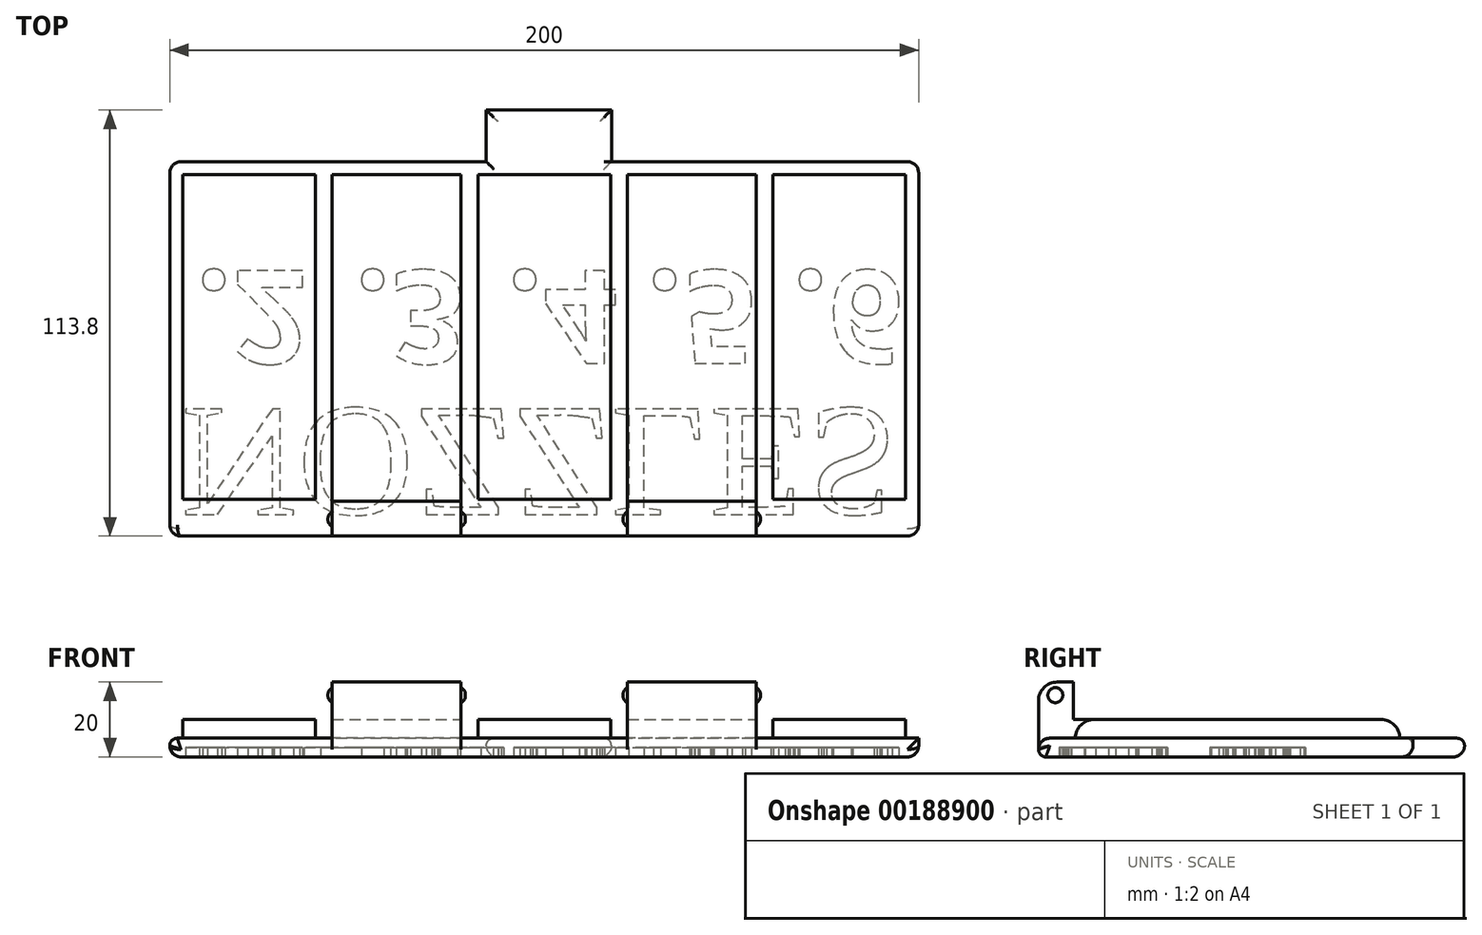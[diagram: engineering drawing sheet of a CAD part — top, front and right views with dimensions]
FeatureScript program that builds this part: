
annotation { "Feature Type Name" : "Feature", "Feature Type Description" : "" }
export const myFeature = defineFeature(function(context is Context, id is Id, definition is map)
    precondition{}
    {
        {
            var Q0;
            Q0=qCreatedBy(makeId("Top.planeOp"),FACE);
            var sketch = newSketch(context, id + "F0", { "sketchPlane" : qUnion([Q0])});
            skLineSegment(sketch, "E0.bottom", {"start": v(-103.4, 30.23) * mm, "end": v(96.6, 30.23) * mm});
            skLineSegment(sketch, "E0.top", {"start": v(-103.4, -69.77) * mm, "end": v(96.6, -69.77) * mm});
            skLineSegment(sketch, "E0.left", {"start": v(-103.4, 30.23) * mm, "end": v(-103.4, -69.77) * mm});
            skLineSegment(sketch, "E0.right", {"start": v(96.6, 30.23) * mm, "end": v(96.6, -69.77) * mm});
            skLineSegment(sketch, "E1.bottom", {"start": v(-18.87, 30.23) * mm, "end": v(14.56, 30.23) * mm});
            skLineSegment(sketch, "E1.top", {"start": v(-18.87, 44.03) * mm, "end": v(14.56, 44.03) * mm});
            skLineSegment(sketch, "E1.left", {"start": v(-18.87, 30.23) * mm, "end": v(-18.87, 44.03) * mm});
            skLineSegment(sketch, "E1.right", {"start": v(14.56, 30.23) * mm, "end": v(14.56, 44.03) * mm});
            skSolve(sketch);
        }
        {
            var Q0;
            Q0=makeQuery(id+"F0.imprint","IMPRINT",FACE,{"disambiguationData":[TD([[makeQuery(id+"F0.imprint","IMPRINT",EDGE,{"derivedFrom":sQuery(id+"F0.wireOp",EDGE,"E0.bottom")}),-1.0]])]});
            var sketch = newSketch(context, id + "F1", { "sketchPlane" : qUnion([Q0])});
            skLineSegment(sketch, "E2.bottom", {"start": v(-99.9, 26.73) * mm, "end": v(-64.5, 26.73) * mm});
            skLineSegment(sketch, "E2.top", {"start": v(-99.9, -59.9) * mm, "end": v(-64.5, -59.9) * mm});
            skLineSegment(sketch, "E2.left", {"start": v(-99.9, 26.73) * mm, "end": v(-99.9, -59.9) * mm});
            skLineSegment(sketch, "E2.right", {"start": v(-64.5, 26.73) * mm, "end": v(-64.5, -59.9) * mm});
            skLineSegment(sketch, "E3.bottom", {"start": v(-60, 26.73) * mm, "end": v(-25.6, 26.73) * mm});
            skLineSegment(sketch, "E3.top", {"start": v(-60, -69.77) * mm, "end": v(-25.6, -69.77) * mm});
            skLineSegment(sketch, "E3.left", {"start": v(-60, 26.73) * mm, "end": v(-60, -69.77) * mm});
            skLineSegment(sketch, "E3.right", {"start": v(-25.6, 26.73) * mm, "end": v(-25.6, -69.77) * mm});
            skLineSegment(sketch, "E4.bottom", {"start": v(-21.1, 26.73) * mm, "end": v(14.3, 26.73) * mm});
            skLineSegment(sketch, "E4.top", {"start": v(-21.1, -59.9) * mm, "end": v(14.3, -59.9) * mm});
            skLineSegment(sketch, "E4.left", {"start": v(-21.1, 26.73) * mm, "end": v(-21.1, -59.9) * mm});
            skLineSegment(sketch, "E4.right", {"start": v(14.3, 26.73) * mm, "end": v(14.3, -59.9) * mm});
            skLineSegment(sketch, "E5.bottom", {"start": v(18.8, 26.73) * mm, "end": v(53.2, 26.73) * mm});
            skLineSegment(sketch, "E5.top", {"start": v(18.8, -69.77) * mm, "end": v(53.2, -69.77) * mm});
            skLineSegment(sketch, "E5.left", {"start": v(18.8, 26.73) * mm, "end": v(18.8, -69.77) * mm});
            skLineSegment(sketch, "E5.right", {"start": v(53.2, 26.73) * mm, "end": v(53.2, -69.77) * mm});
            skLineSegment(sketch, "E6.bottom", {"start": v(57.7, 26.73) * mm, "end": v(93.1, 26.73) * mm});
            skLineSegment(sketch, "E6.top", {"start": v(57.7, -59.9) * mm, "end": v(93.1, -59.9) * mm});
            skLineSegment(sketch, "E6.left", {"start": v(57.7, 26.73) * mm, "end": v(57.7, -59.9) * mm});
            skLineSegment(sketch, "E6.right", {"start": v(93.1, 26.73) * mm, "end": v(93.1, -59.9) * mm});
            skSolve(sketch);
        }
        {
            var Q0;
            Q0 = qSketchRegion(id + "F0", true);
            extrude(context, id + "F2", {"entities" : qUnion([Q0]), "depth" : 5 * mm});
        }
        {
            var Q0;
            Q0 = qSketchRegion(id + "F1", true);
            extrude(context, id + "F3", {"entities" : qUnion([Q0]), "operationType" : NewBodyOperationType.ADD, "depth" : 10 * mm});
        }
        {
            var Q0;
            Q0=makeQuery(id+"F3.opExtrude","CAP_EDGE",EDGE,{"disambiguationData":[OSD([sQuery(id+"F1.wireOp",EDGE,"E2.top")])],"isStart":false});
            var Q1;
            Q1=makeQuery(id+"F3.opExtrude","CAP_EDGE",EDGE,{"disambiguationData":[OSD([sQuery(id+"F1.wireOp",EDGE,"E4.top")])],"isStart":false});
            var Q2;
            Q2=makeQuery(id+"F3.opExtrude","CAP_EDGE",EDGE,{"disambiguationData":[OSD([sQuery(id+"F1.wireOp",EDGE,"E6.top")])],"isStart":false});
            var Q3;
            Q3=makeQuery(id+"F3.opExtrude","CAP_EDGE",EDGE,{"disambiguationData":[OSD([sQuery(id+"F1.wireOp",EDGE,"E2.bottom")])],"isStart":false});
            var Q4;
            Q4=makeQuery(id+"F3.opExtrude","CAP_EDGE",EDGE,{"disambiguationData":[OSD([sQuery(id+"F1.wireOp",EDGE,"E3.bottom")])],"isStart":false});
            var Q5;
            Q5=makeQuery(id+"F3.opExtrude","CAP_EDGE",EDGE,{"disambiguationData":[OSD([sQuery(id+"F1.wireOp",EDGE,"E4.bottom")])],"isStart":false});
            var Q6;
            Q6=makeQuery(id+"F3.opExtrude","CAP_EDGE",EDGE,{"disambiguationData":[OSD([sQuery(id+"F1.wireOp",EDGE,"E5.bottom")])],"isStart":false});
            var Q7;
            Q7=makeQuery(id+"F3.opExtrude","CAP_EDGE",EDGE,{"disambiguationData":[OSD([sQuery(id+"F1.wireOp",EDGE,"E6.bottom")])],"isStart":false});
            fillet(context, id + "F4", {"entities" : qUnion([Q0, Q1, Q2, Q3, Q4, Q5, Q6, Q7]), "radius" : 5 * mm, "tangentPropagation" : true, "allowEdgeOverflow" : false});
        }
        {
            var Q0;
            Q0=makeQuery(id+"F2.opExtrude","CAP_EDGE",EDGE,{"disambiguationData":[OSD([sQuery(id+"F0.wireOp",EDGE,"E0.left")])],"isStart":true});
            var Q1;
            Q1=makeQuery(id+"F2.opExtrude","SWEPT_EDGE",EDGE,{"disambiguationData":[OSD([sQuery(id+"F0.wireOp",EDGE,"E0.top"),sQuery(id+"F0.wireOp",EDGE,"E0.left")])]});
            var Q2;
            Q2=makeQuery(id+"F2.opExtrude","SWEPT_EDGE",EDGE,{"disambiguationData":[OSD([sQuery(id+"F0.wireOp",EDGE,"E0.top"),sQuery(id+"F0.wireOp",EDGE,"E0.right")])]});
            var Q3;
            Q3=makeQuery(id+"F2.opExtrude","CAP_EDGE",EDGE,{"disambiguationData":[OSD([sQuery(id+"F0.wireOp",EDGE,"E0.right")])],"isStart":true});
            var Q4;
            Q4=makeQuery(id+"F2.opExtrude","SWEPT_EDGE",EDGE,{"disambiguationData":[OSD([sQuery(id+"F0.wireOp",EDGE,"E0.bottom"),sQuery(id+"F0.wireOp",EDGE,"E0.right")])]});
            var Q5;
            Q5=makeQuery(id+"F2.opExtrude","CAP_EDGE",EDGE,{"disambiguationData":[OSD([sQuery(id+"F0.wireOp",EDGE,"E0.bottom")])],"isStart":true});
            var Q6;
            Q6=makeQuery(id+"F2.opExtrude","SWEPT_EDGE",EDGE,{"disambiguationData":[OSD([sQuery(id+"F0.wireOp",EDGE,"E0.bottom"),sQuery(id+"F0.wireOp",EDGE,"E0.left")])]});
            var Q7;
            Q7=makeQuery(id+"F2.opExtrude","CAP_EDGE",EDGE,{"disambiguationData":[OSD([sQuery(id+"F0.wireOp",EDGE,"E1.right")])],"isStart":true});
            var Q8;
            Q8=makeQuery(id+"F2.opExtrude","CAP_EDGE",EDGE,{"disambiguationData":[OSD([sQuery(id+"F0.wireOp",EDGE,"E1.top")])],"isStart":true});
            var Q9;
            Q9=makeQuery(id+"F2.opExtrude","CAP_EDGE",EDGE,{"disambiguationData":[OSD([sQuery(id+"F0.wireOp",EDGE,"E1.left")])],"isStart":true});
            var Q10;
            {var subQ0=sQuery(id+"F0.wireOp",EDGE,"E0.right");var subQ1=sQuery(id+"F0.wireOp",EDGE,"E0.top");Q10=makeQuery(id+"F3.boolean.opBoolean","SPLIT",EDGE,{"disambiguationData":[TD([makeQuery(id+"F2.opExtrude","SWEPT_FACE",FACE,{"disambiguationData":[OSD([subQ0])]})])],"derivedFrom":makeQuery(id+"F2.opExtrude","CAP_EDGE",EDGE,{"disambiguationData":[OSD([subQ1])],"isStart":false})});}
            var Q11;
            {var subQ0=sQuery(id+"F0.wireOp",EDGE,"E0.top");Q11=makeQuery(id+"F3.boolean.opBoolean","SPLIT",EDGE,{"disambiguationData":[TD([makeQuery(id+"F3.opExtrude","SWEPT_FACE",FACE,{"disambiguationData":[OSD([sQuery(id+"F1.wireOp",EDGE,"E3.right")])]})])],"derivedFrom":makeQuery(id+"F2.opExtrude","CAP_EDGE",EDGE,{"disambiguationData":[OSD([subQ0])],"isStart":false})});}
            var Q12;
            {var subQ0=sQuery(id+"F0.wireOp",EDGE,"E0.left");var subQ1=sQuery(id+"F0.wireOp",EDGE,"E0.top");Q12=makeQuery(id+"F3.boolean.opBoolean","SPLIT",EDGE,{"disambiguationData":[TD([makeQuery(id+"F2.opExtrude","SWEPT_FACE",FACE,{"disambiguationData":[OSD([subQ0])]})])],"derivedFrom":makeQuery(id+"F2.opExtrude","CAP_EDGE",EDGE,{"disambiguationData":[OSD([subQ1])],"isStart":false})});}
            fillet(context, id + "F5", {"entities" : qUnion([Q0, Q1, Q2, Q3, Q4, Q5, Q6, Q7, Q8, Q9, Q10, Q11, Q12]), "radius" : 3 * mm, "tangentPropagation" : true, "allowEdgeOverflow" : false});
        }
        {
            var Q0;
            Q0=makeQuery(id+"F2.opExtrude","CAP_FACE",FACE,{"disambiguationData":[OSD([sQuery(id+"F0.wireOp",EDGE,"E0.bottom"),sQuery(id+"F0.wireOp",EDGE,"E0.top"),sQuery(id+"F0.wireOp",EDGE,"E0.left"),sQuery(id+"F0.wireOp",EDGE,"E0.right")])],"isStart":true});
            var sketch = newSketch(context, id + "F6", { "sketchPlane" : qUnion([Q0])});
            skLineSegment(sketch, "E7.left", {"start": v(-96.6, 23.86) * mm, "end": v(-96.6, -1.14) * mm});
            skLineSegment(sketch, "E7.right", {"start": v(-60.2, 23.86) * mm, "end": v(-60.2, -1.14) * mm});
            skLineSegment(sketch, "E8.left", {"start": v(-57.2, 23.86) * mm, "end": v(-57.2, -1.14) * mm});
            skLineSegment(sketch, "E8.right", {"start": v(-20.8, 23.86) * mm, "end": v(-20.8, -1.14) * mm});
            skLineSegment(sketch, "E9.left", {"start": v(-17.8, 23.86) * mm, "end": v(-17.8, -1.14) * mm});
            skLineSegment(sketch, "E9.right", {"start": v(18.6, 23.86) * mm, "end": v(18.6, -1.14) * mm});
            skLineSegment(sketch, "E10.right", {"start": v(58, 23.86) * mm, "end": v(58, -1.14) * mm});
            skLineSegment(sketch, "E11.left", {"start": v(61, 23.86) * mm, "end": v(61, -1.14) * mm});
            skLineSegment(sketch, "E12", {"start": v(-96.6, 23.86) * mm, "end": v(58, 23.86) * mm, "construction": true});
            skLineSegment(sketch, "E13", {"start": v(-96.6, -1.14) * mm, "end": v(61, -1.14) * mm, "construction": true});
            skText(sketch, "E14", { "text": ".2", "fontName": "OpenSans-Bold.ttf"});
            skText(sketch, "E15", { "text": ".3", "fontName": "OpenSans-Bold.ttf"});
            skText(sketch, "E16", { "text": ".4", "fontName": "OpenSans-Bold.ttf"});
            skText(sketch, "E17", { "text": ".5", "fontName": "OpenSans-Bold.ttf"});
            skText(sketch, "E18", { "text": ".6", "fontName": "OpenSans-Bold.ttf"});
            skPoint(sketch, "E19.orphan", {"position": v(-60.2, -46.1) * mm});
            skPoint(sketch, "E9.top.end.orphan", {"position": v(18.6, -46.1) * mm});
            skPoint(sketch, "E8.top.end.orphan", {"position": v(-20.8, -46.1) * mm});
            skPoint(sketch, "E20.orphan", {"position": v(58, -46.1) * mm});
            skPoint(sketch, "E21.orphan", {"position": v(58, 46.05) * mm});
            skPoint(sketch, "E11.bottom.start.orphan", {"position": v(61, 46.05) * mm});
            skPoint(sketch, "E22.orphan", {"position": v(97.4, -46.1) * mm});
            skText(sketch, "E23", { "text": "NOZZLES", "fontName": "Tinos-Regular.ttf"});
            const initialGuessF6  = {"E14": [-0.0966, -0.00114, 1, 0, 0.025], "E15": [-0.05416, -0.00114, 1, 0, 0.025], "E16": [-0.01353, -0.00114, 1, 0, 0.025], "E17": [0.02382, -0.00114, 1, 0, 0.025], "E18": [0.06272, -0.00114, 1, 0, 0.025], "E23": [-0.1004, 0.03577, 1, 0, 0.031]};
            skSetInitialGuess(sketch, initialGuessF6);
            skSolve(sketch);
        }
        {
            var Q0;
            Q0 = qSketchRegion(id + "F6", true);
            extrude(context, id + "F7", {"entities" : qUnion([Q0]), "operationType" : NewBodyOperationType.REMOVE, "oppositeDirection" : true, "depth" : 2.5 * mm});
        }
        {
            var Q0;
            Q0=makeQuery(id+"F3.opExtrude","CAP_FACE",FACE,{"disambiguationData":[OSD([sQuery(id+"F1.wireOp",EDGE,"E5.bottom"),sQuery(id+"F1.wireOp",EDGE,"E5.top"),sQuery(id+"F1.wireOp",EDGE,"E5.left"),sQuery(id+"F1.wireOp",EDGE,"E5.right")])],"isStart":false});
            var sketch = newSketch(context, id + "F8", { "sketchPlane" : qUnion([Q0])});
            skLineSegment(sketch, "E24.bottom", {"start": v(-25.6, -69.77) * mm, "end": v(-29.6, -69.77) * mm});
            skLineSegment(sketch, "E24.top", {"start": v(-25.6, -60.4) * mm, "end": v(-29.6, -60.4) * mm});
            skLineSegment(sketch, "E24.left", {"start": v(-25.6, -69.77) * mm, "end": v(-25.6, -60.4) * mm});
            skLineSegment(sketch, "E24.right", {"start": v(-60, -69.77) * mm, "end": v(-60, -60.4) * mm});
            skLineSegment(sketch, "E25.trimOffspring", {"start": v(-32.6, -69.77) * mm, "end": v(-53, -69.77) * mm});
            skLineSegment(sketch, "E26.trimOffspring", {"start": v(-32.6, -60.4) * mm, "end": v(-53, -60.4) * mm});
            skLineSegment(sketch, "E27.trimOffspring", {"start": v(-56, -60.4) * mm, "end": v(-60, -60.4) * mm});
            skLineSegment(sketch, "E28.trimOffspring", {"start": v(-56, -69.77) * mm, "end": v(-60, -69.77) * mm});
            skLineSegment(sketch, "E29", {"start": v(-56, -60.4) * mm, "end": v(-53, -60.4) * mm});
            skLineSegment(sketch, "E30", {"start": v(-53, -69.77) * mm, "end": v(-56, -69.77) * mm});
            skLineSegment(sketch, "E31", {"start": v(-32.6, -60.4) * mm, "end": v(-29.6, -60.4) * mm});
            skLineSegment(sketch, "E32", {"start": v(-29.6, -69.77) * mm, "end": v(-32.6, -69.77) * mm});
            skLineSegment(sketch, "E33.bottom", {"start": v(18.8, -60.4) * mm, "end": v(53.2, -60.4) * mm});
            skLineSegment(sketch, "E33.top", {"start": v(18.8, -69.77) * mm, "end": v(53.2, -69.77) * mm});
            skLineSegment(sketch, "E33.left", {"start": v(18.8, -60.4) * mm, "end": v(18.8, -69.77) * mm});
            skLineSegment(sketch, "E33.right", {"start": v(53.2, -60.4) * mm, "end": v(53.2, -69.77) * mm});
            skSolve(sketch);
        }
        {
            var Q0;
            Q0 = qSketchRegion(id + "F8", true);
            extrude(context, id + "F9", {"entities" : qUnion([Q0]), "operationType" : NewBodyOperationType.ADD, "depth" : 10 * mm});
        }
        {
            var Q0;
            Q0=makeQuery(id+"F9.opExtrude","CAP_EDGE",EDGE,{"disambiguationData":[OSD([sQuery(id+"F8.wireOp",EDGE,"E24.bottom")])],"isStart":false});
            var Q1;
            Q1=makeQuery(id+"F9.opExtrude","CAP_EDGE",EDGE,{"disambiguationData":[OSD([sQuery(id+"F8.wireOp",EDGE,"fa0df908-ae73-434e-80fb-e9a63f663edb.bottom")])],"isStart":false});
            var Q2;
            Q2=makeQuery(id+"F9.opExtrude","CAP_EDGE",EDGE,{"disambiguationData":[OSD([sQuery(id+"F8.wireOp",EDGE,"E25.trimOffspring")])],"isStart":false});
            var Q3;
            Q3=makeQuery(id+"F9.opExtrude","CAP_EDGE",EDGE,{"disambiguationData":[OSD([sQuery(id+"F8.wireOp",EDGE,"E28.trimOffspring")])],"isStart":false});
            var Q4;
            Q4=makeQuery(id+"F9.opExtrude","CAP_EDGE",EDGE,{"disambiguationData":[OSD([sQuery(id+"F8.wireOp",EDGE,"31049aec-f189-481b-be80-5d468b2427ca.trimOffspring")])],"isStart":false});
            var Q5;
            Q5=makeQuery(id+"F9.opExtrude","CAP_EDGE",EDGE,{"disambiguationData":[OSD([sQuery(id+"F8.wireOp",EDGE,"0924c1d6-45e6-4c9e-b806-b59c634f07b1.trimOffspring")])],"isStart":false});
            var Q6;
            Q6=makeQuery(id+"F9.opExtrude","CAP_EDGE",EDGE,{"disambiguationData":[OSD([sQuery(id+"F8.wireOp",EDGE,"E33.top")])],"isStart":false});
            fillet(context, id + "F10", {"entities" : qUnion([Q0, Q1, Q2, Q3, Q4, Q5, Q6]), "radius" : 5 * mm, "tangentPropagation" : true, "allowEdgeOverflow" : false});
        }
        {
            var Q0;
            Q0=makeQuery(id+"F9.boolean.opBoolean","MERGE",FACE,{"derivedFrom":[makeQuery(id+"F3.opExtrude","SWEPT_FACE",FACE,{"disambiguationData":[OSD([sQuery(id+"F1.wireOp",EDGE,"E3.left")])]}),makeQuery(id+"F9.opExtrude","SWEPT_FACE",FACE,{"disambiguationData":[OSD([sQuery(id+"F8.wireOp",EDGE,"E24.right")])]})]});
            var sketch = newSketch(context, id + "F11", { "sketchPlane" : qUnion([Q0])});
            skCircle(sketch, "E34", {"center": v(65.27, 16.5) * mm, "radius": 2 * mm});
            skSolve(sketch);
        }
        {
            var Q0;
            Q0=makeQuery(id+"F9.boolean.opBoolean","MERGE",FACE,{"derivedFrom":[makeQuery(id+"F3.opExtrude","SWEPT_FACE",FACE,{"disambiguationData":[OSD([sQuery(id+"F1.wireOp",EDGE,"E3.right")])]}),makeQuery(id+"F9.opExtrude","SWEPT_FACE",FACE,{"disambiguationData":[OSD([sQuery(id+"F8.wireOp",EDGE,"E24.left")])]})]});
            var sketch = newSketch(context, id + "F12", { "sketchPlane" : qUnion([Q0])});
            skCircle(sketch, "E35", {"center": v(-65.27, 16.5) * mm, "radius": 2 * mm});
            skSolve(sketch);
        }
        {
            var Q0;
            Q0=makeQuery(id+"F9.boolean.opBoolean","MERGE",FACE,{"derivedFrom":[makeQuery(id+"F3.opExtrude","SWEPT_FACE",FACE,{"disambiguationData":[OSD([sQuery(id+"F1.wireOp",EDGE,"E5.right")])]}),makeQuery(id+"F9.opExtrude","SWEPT_FACE",FACE,{"disambiguationData":[OSD([sQuery(id+"F8.wireOp",EDGE,"fa0df908-ae73-434e-80fb-e9a63f663edb.left")])]})]});
            var sketch = newSketch(context, id + "F13", { "sketchPlane" : qUnion([Q0])});
            skCircle(sketch, "E36", {"center": v(-65.27, 16.5) * mm, "radius": 2 * mm});
            skSolve(sketch);
        }
        {
            var Q0;
            Q0=makeQuery(id+"F9.boolean.opBoolean","MERGE",FACE,{"derivedFrom":[makeQuery(id+"F3.opExtrude","SWEPT_FACE",FACE,{"disambiguationData":[OSD([sQuery(id+"F1.wireOp",EDGE,"E5.left")])]}),makeQuery(id+"F9.opExtrude","SWEPT_FACE",FACE,{"disambiguationData":[OSD([sQuery(id+"F8.wireOp",EDGE,"fa0df908-ae73-434e-80fb-e9a63f663edb.right")])]})]});
            var sketch = newSketch(context, id + "F14", { "sketchPlane" : qUnion([Q0])});
            skCircle(sketch, "E37", {"center": v(65.27, 16.5) * mm, "radius": 2 * mm});
            skSolve(sketch);
        }
        {
            var Q0;
            Q0=makeQuery(id+"F11.imprint","IMPRINT",FACE,{"disambiguationData":[TD([[makeQuery(id+"F11.imprint","IMPRINT",EDGE,{"derivedFrom":sQuery(id+"F11.wireOp",EDGE,"E34")}),1.0]])]});
            var Q1;
            Q1=makeQuery(id+"F14.imprint","IMPRINT",FACE,{"disambiguationData":[TD([[makeQuery(id+"F14.imprint","IMPRINT",EDGE,{"derivedFrom":sQuery(id+"F14.wireOp",EDGE,"E37")}),1.0]])]});
            var Q2;
            Q2=makeQuery(id+"F13.imprint","IMPRINT",FACE,{"disambiguationData":[TD([[makeQuery(id+"F13.imprint","IMPRINT",EDGE,{"derivedFrom":sQuery(id+"F13.wireOp",EDGE,"E36")}),1.0]])]});
            var Q3;
            Q3=makeQuery(id+"F12.imprint","IMPRINT",FACE,{"disambiguationData":[TD([[makeQuery(id+"F12.imprint","IMPRINT",EDGE,{"derivedFrom":sQuery(id+"F12.wireOp",EDGE,"E35")}),1.0]])]});
            extrude(context, id + "F15", {"entities" : qUnion([Q0, Q1, Q2, Q3]), "operationType" : NewBodyOperationType.ADD, "endBound" : BoundingType.SYMMETRIC, "depth" : 2.3 * mm});
        }
        {
            var Q0;
            Q0=makeQuery(id+"F15.opExtrude","CAP_EDGE",EDGE,{"disambiguationData":[OSD([sQuery(id+"F11.wireOp",EDGE,"E34")])],"isStart":false});
            var Q1;
            Q1=makeQuery(id+"F15.opExtrude","CAP_EDGE",EDGE,{"disambiguationData":[OSD([sQuery(id+"F14.wireOp",EDGE,"E37")])],"isStart":false});
            var Q2;
            Q2=makeQuery(id+"F15.opExtrude","CAP_EDGE",EDGE,{"disambiguationData":[OSD([sQuery(id+"F12.wireOp",EDGE,"E35")])],"isStart":true});
            var Q3;
            Q3=makeQuery(id+"F15.opExtrude","CAP_EDGE",EDGE,{"disambiguationData":[OSD([sQuery(id+"F13.wireOp",EDGE,"E36")])],"isStart":true});
            fillet(context, id + "F16", {"entities" : qUnion([Q0, Q1, Q2, Q3]), "radius" : 2 * mm, "tangentPropagation" : true, "allowEdgeOverflow" : false});
        }
        {
            var Q0;
            Q0=makeQuery(id+"F2.opExtrude","CAP_EDGE",EDGE,{"disambiguationData":[OSD([sQuery(id+"F0.wireOp",EDGE,"E0.left")])],"isStart":false});
            var Q1;
            {var subQ0=sQuery(id+"F0.wireOp",EDGE,"E0.left");var subQ1=sQuery(id+"F0.wireOp",EDGE,"E0.top");Q1=makeQuery(id+"F3.boolean.opBoolean","SPLIT",EDGE,{"disambiguationData":[TD([makeQuery(id+"F2.opExtrude","SWEPT_FACE",FACE,{"disambiguationData":[OSD([subQ0])]})])],"derivedFrom":makeQuery(id+"F2.opExtrude","CAP_EDGE",EDGE,{"disambiguationData":[OSD([subQ1])],"isStart":false})});}
            var Q2;
            {var subQ0=sQuery(id+"F0.wireOp",EDGE,"E0.left");var subQ1=sQuery(id+"F0.wireOp",EDGE,"E0.top");Q2=makeQuery(id+"F5.opFillet","BLEND_EDGE",EDGE,{"blendedFrom":[makeQuery(id+"F2.opExtrude","SWEPT_EDGE",EDGE,{"disambiguationData":[OSD([subQ1,subQ0])]}),makeQuery(id+"F2.opExtrude","CAP_FACE",FACE,{"disambiguationData":[OSD([sQuery(id+"F0.wireOp",EDGE,"E0.bottom"),subQ1,subQ0,sQuery(id+"F0.wireOp",EDGE,"E0.right"),sQuery(id+"F0.wireOp",EDGE,"E1.top"),sQuery(id+"F0.wireOp",EDGE,"E1.left"),sQuery(id+"F0.wireOp",EDGE,"E1.right")])],"isStart":false})],"blendedInto":[makeQuery(id+"F2.opExtrude","CAP_FACE",FACE,{"disambiguationData":[OSD([sQuery(id+"F0.wireOp",EDGE,"E0.bottom"),subQ1,subQ0,sQuery(id+"F0.wireOp",EDGE,"E0.right"),sQuery(id+"F0.wireOp",EDGE,"E1.top"),sQuery(id+"F0.wireOp",EDGE,"E1.left"),sQuery(id+"F0.wireOp",EDGE,"E1.right")])],"isStart":false})]});}
            var Q3;
            {var subQ0=sQuery(id+"F0.wireOp",EDGE,"E0.left");var subQ1=sQuery(id+"F0.wireOp",EDGE,"E0.bottom");Q3=makeQuery(id+"F5.opFillet","BLEND_EDGE",EDGE,{"blendedFrom":[makeQuery(id+"F2.opExtrude","SWEPT_EDGE",EDGE,{"disambiguationData":[OSD([subQ1,subQ0])]}),makeQuery(id+"F2.opExtrude","CAP_FACE",FACE,{"disambiguationData":[OSD([subQ1,sQuery(id+"F0.wireOp",EDGE,"E0.top"),subQ0,sQuery(id+"F0.wireOp",EDGE,"E0.right"),sQuery(id+"F0.wireOp",EDGE,"E1.top"),sQuery(id+"F0.wireOp",EDGE,"E1.left"),sQuery(id+"F0.wireOp",EDGE,"E1.right")])],"isStart":false})],"blendedInto":[makeQuery(id+"F2.opExtrude","CAP_FACE",FACE,{"disambiguationData":[OSD([subQ1,sQuery(id+"F0.wireOp",EDGE,"E0.top"),subQ0,sQuery(id+"F0.wireOp",EDGE,"E0.right"),sQuery(id+"F0.wireOp",EDGE,"E1.top"),sQuery(id+"F0.wireOp",EDGE,"E1.left"),sQuery(id+"F0.wireOp",EDGE,"E1.right")])],"isStart":false})]});}
            var Q4;
            {var subQ0=sQuery(id+"F0.wireOp",EDGE,"E0.bottom");Q4=makeQuery(id+"F2.opExtrude","CAP_EDGE",EDGE,{"disambiguationData":[OSD([subQ0]),TDD([makeQuery(id+"F0.imprint","IMPRINT",EDGE,{"disambiguationData":[TD([[makeQuery(id+"F0.imprint","INTERSECT",VERTEX,{"derivedFrom":[subQ0,sQuery(id+"F0.wireOp",EDGE,"E0.left")]}),-1.0]])],"derivedFrom":subQ0})])],"isStart":false});}
            var Q5;
            Q5=makeQuery(id+"F2.opExtrude","CAP_EDGE",EDGE,{"disambiguationData":[OSD([sQuery(id+"F0.wireOp",EDGE,"E1.left")])],"isStart":false});
            var Q6;
            Q6=makeQuery(id+"F2.opExtrude","CAP_EDGE",EDGE,{"disambiguationData":[OSD([sQuery(id+"F0.wireOp",EDGE,"E1.top")])],"isStart":false});
            var Q7;
            Q7=makeQuery(id+"F2.opExtrude","CAP_EDGE",EDGE,{"disambiguationData":[OSD([sQuery(id+"F0.wireOp",EDGE,"E1.right")])],"isStart":false});
            var Q8;
            Q8=makeQuery(id+"F2.opExtrude","CAP_EDGE",EDGE,{"disambiguationData":[OSD([sQuery(id+"F0.wireOp",EDGE,"E0.top")])],"isStart":true});
            fillet(context, id + "F17", {"entities" : qUnion([Q0, Q1, Q2, Q3, Q4, Q5, Q6, Q7, Q8]), "radius" : 2 * mm, "tangentPropagation" : true, "allowEdgeOverflow" : false});
        }
    });
